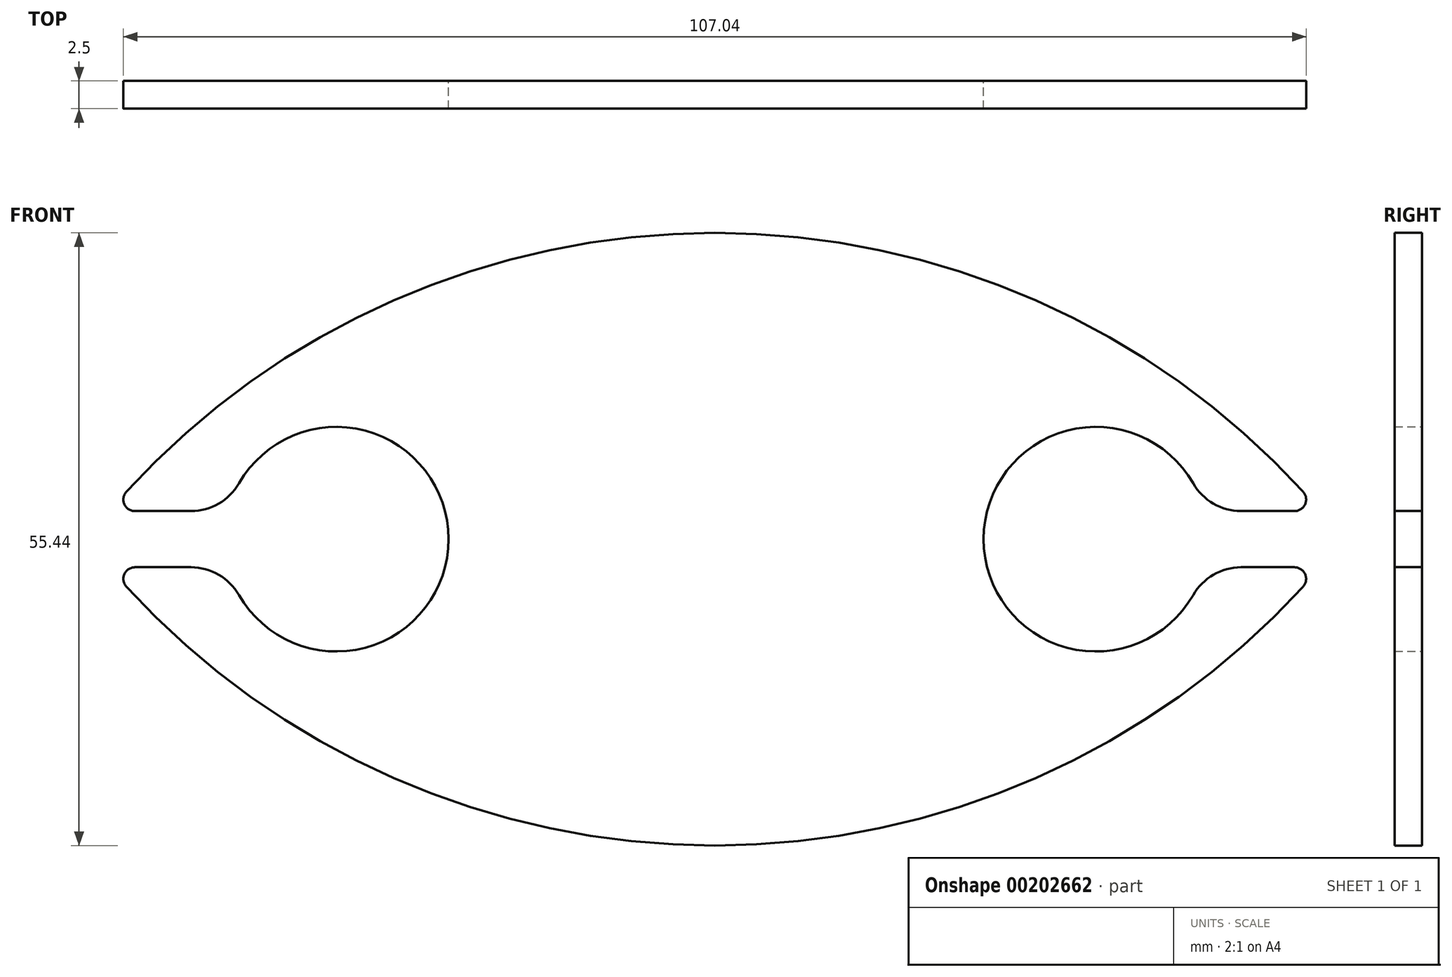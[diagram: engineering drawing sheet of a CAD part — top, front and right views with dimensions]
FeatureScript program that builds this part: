
annotation { "Feature Type Name" : "Feature", "Feature Type Description" : "" }
export const myFeature = defineFeature(function(context is Context, id is Id, definition is map)
    precondition{}
    {
        {
            var Q0;
            Q0=qCreatedBy(makeId("Front.planeOp"),FACE);
            var sketch = newSketch(context, id + "F0", { "sketchPlane" : qUnion([Q0])});
            skArc(sketch, "E0", {"start": v(18, 10.47) * mm, "mid": v(-35.24, 33.88) * mm, "end": v(-88.48, 10.47) * mm});
            skCircle(sketch, "E1", {"center": v(-69.49, 6.16) * mm, "radius": 10.16 * mm});
            skCircle(sketch, "E2.MirrorC", {"center": v(-0.75, 6.16) * mm, "radius": 10.16 * mm});
            skLineSegment(sketch, "E3", {"start": v(-87.7, 8.7) * mm, "end": v(-79.33, 8.7) * mm});
            skPoint(sketch, "E4.orphan", {"position": v(20.64, 7.43) * mm});
            skPoint(sketch, "E5.orphan", {"position": v(-91.12, 7.43) * mm});
            skArc(sketch, "E6.MirrorCS", {"start": v(18, 1.85) * mm, "mid": v(-35.24, -21.56) * mm, "end": v(-88.48, 1.85) * mm});
            skLineSegment(sketch, "E7.MirrorCS", {"start": v(-87.7, 3.62) * mm, "end": v(-79.33, 3.62) * mm});
            skLineSegment(sketch, "E8.trimOffspring", {"start": v(9.09, 8.7) * mm, "end": v(17.22, 8.7) * mm});
            skLineSegment(sketch, "E9.trimOffspring", {"start": v(9.09, 3.62) * mm, "end": v(17.22, 3.62) * mm});
            skPoint(sketch, "E10.visualSharp", {"position": v(-90.05, 3.62) * mm});
            skArc(sketch, "E10.filletArc", {"start": v(-87.7, 3.62) * mm, "mid": v(-88.67, 3) * mm, "end": v(-88.48, 1.85) * mm});
            skPoint(sketch, "E11.visualSharp", {"position": v(19.57, 3.62) * mm});
            skArc(sketch, "E11.filletArc", {"start": v(18, 1.85) * mm, "mid": v(18.2, 3) * mm, "end": v(17.22, 3.62) * mm});
            skPoint(sketch, "E12.visualSharp", {"position": v(19.57, 8.7) * mm});
            skArc(sketch, "E12.filletArc", {"start": v(17.22, 8.7) * mm, "mid": v(18.2, 9.33) * mm, "end": v(18, 10.47) * mm});
            skPoint(sketch, "E13.visualSharp", {"position": v(-90.05, 8.7) * mm});
            skArc(sketch, "E13.filletArc", {"start": v(-88.48, 10.47) * mm, "mid": v(-88.67, 9.33) * mm, "end": v(-87.7, 8.7) * mm});
            skPoint(sketch, "E14.orphan", {"position": v(-35.24, 7.43) * mm});
            skSolve(sketch);
        }
        {
            var Q0;
            Q0=makeQuery(id+"F0.imprint","IMPRINT",FACE,{"disambiguationData":[TD([[makeQuery(id+"F0.imprint","IMPRINT",EDGE,{"derivedFrom":sQuery(id+"F0.wireOp",EDGE,"E0")}),1.0]])]});
            extrude(context, id + "F1", {"entities" : qUnion([Q0]), "depth" : 2.5 * mm});
        }
        {
            var Q0;
            Q0=makeQuery(id+"F1.opExtrude","SWEPT_EDGE",EDGE,{"disambiguationData":[OSD([sQuery(id+"F0.wireOp",EDGE,"E1"),sQuery(id+"F0.wireOp",EDGE,"E7.MirrorCS")])]});
            var Q1;
            Q1=makeQuery(id+"F1.opExtrude","SWEPT_EDGE",EDGE,{"disambiguationData":[OSD([sQuery(id+"F0.wireOp",EDGE,"E1"),sQuery(id+"F0.wireOp",EDGE,"E3")])]});
            var Q2;
            Q2=makeQuery(id+"F1.opExtrude","SWEPT_EDGE",EDGE,{"disambiguationData":[OSD([sQuery(id+"F0.wireOp",EDGE,"E2.MirrorC"),sQuery(id+"F0.wireOp",EDGE,"E8.trimOffspring")])]});
            var Q3;
            Q3=makeQuery(id+"F1.opExtrude","SWEPT_EDGE",EDGE,{"disambiguationData":[OSD([sQuery(id+"F0.wireOp",EDGE,"E2.MirrorC"),sQuery(id+"F0.wireOp",EDGE,"E9.trimOffspring")])]});
            fillet(context, id + "F2", {"entities" : qUnion([Q0, Q1, Q2, Q3]), "radius" : 5 * mm, "tangentPropagation" : true, "allowEdgeOverflow" : false});
        }
    });
